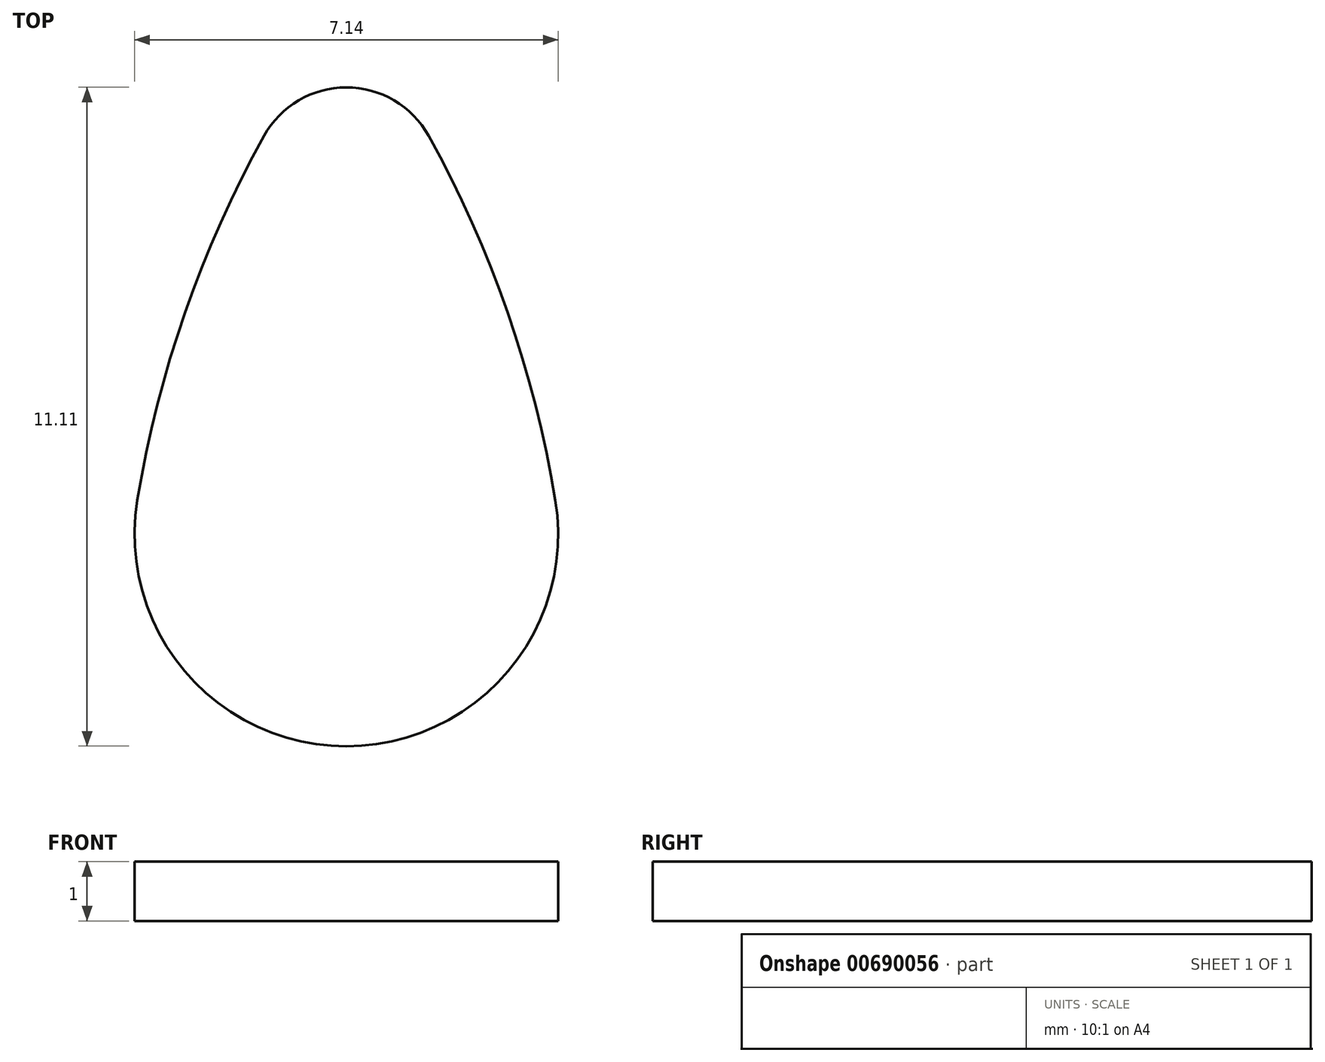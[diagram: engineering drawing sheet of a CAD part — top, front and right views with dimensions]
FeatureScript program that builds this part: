
annotation { "Feature Type Name" : "Feature", "Feature Type Description" : "" }
export const myFeature = defineFeature(function(context is Context, id is Id, definition is map)
    precondition{}
    {
        {
            var Q0;
            Q0=qCreatedBy(makeId("Top.planeOp"),FACE);
            var sketch = newSketch(context, id + "F0", { "sketchPlane" : qUnion([Q0])});
            skArc(sketch, "E0", {"start": v(-3.52, -0.41) * mm, "mid": v(0, -4.56) * mm, "end": v(3.52, -0.41) * mm});
            skArc(sketch, "E1", {"start": v(1.39, 5.73) * mm, "mid": v(0, 6.55) * mm, "end": v(-1.39, 5.73) * mm});
            skArc(sketch, "E2", {"start": v(-1.39, 5.73) * mm, "mid": v(-2.72, 2.75) * mm, "end": v(-3.52, -0.41) * mm});
            skArc(sketch, "E3", {"start": v(3.52, -0.41) * mm, "mid": v(2.72, 2.75) * mm, "end": v(1.39, 5.73) * mm});
            skPoint(sketch, "E4", {"position": v(0, 6.55) * mm});
            skPoint(sketch, "E4.positionSnap0", {"position": v(0, 6.55) * mm});
            skPoint(sketch, "E5", {"position": v(0, -4.56) * mm});
            skLineSegment(sketch, "E6", {"start": v(-3.57, -1) * mm, "end": v(3.57, -1) * mm, "construction": true});
            skLineSegment(sketch, "E7", {"start": v(0, -4.56) * mm, "end": v(0, 6.55) * mm, "construction": true});
            skPoint(sketch, "E8", {"position": v(0, 1) * mm});
            skLineSegment(sketch, "E9", {"start": v(0, -1) * mm, "end": v(0, 1) * mm, "construction": true});
            skPoint(sketch, "E10", {"position": v(0, 0) * mm});
            skSolve(sketch);
        }
        {
            var Q0;
            Q0 = qSketchRegion(id + "F0", true);
            extrude(context, id + "F1", {"entities" : qUnion([Q0]), "depth" : 1 * mm, "offsetDistance" : 25.4 * mm});
        }
    });
